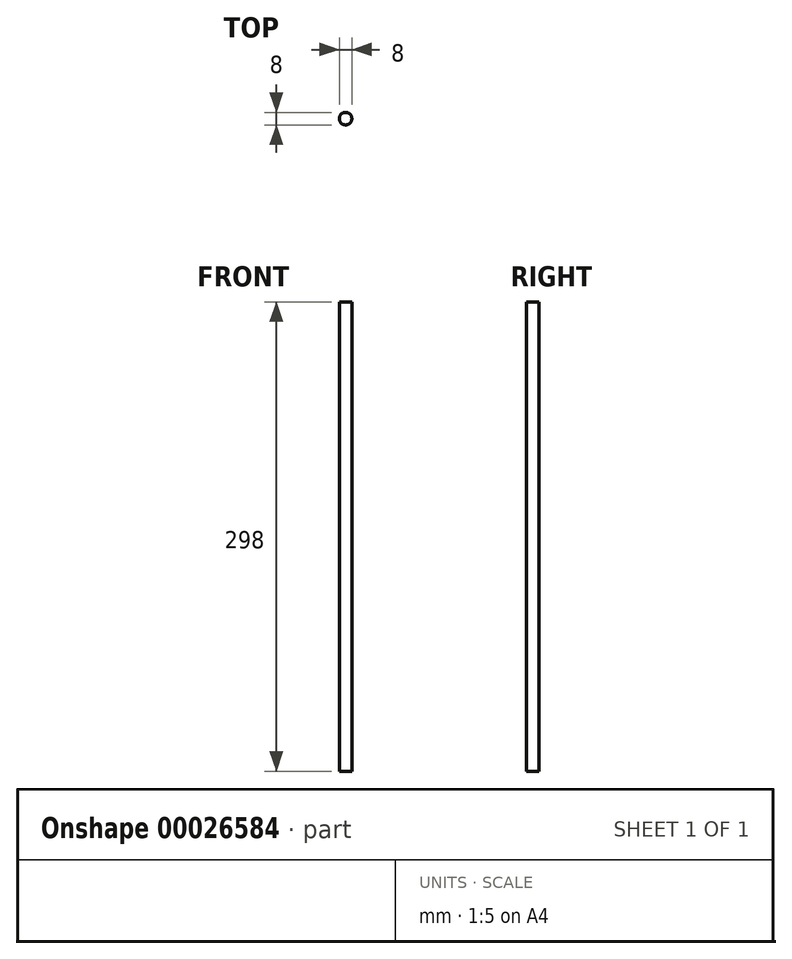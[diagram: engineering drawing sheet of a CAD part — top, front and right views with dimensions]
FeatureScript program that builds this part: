
annotation { "Feature Type Name" : "Feature", "Feature Type Description" : "" }
export const myFeature = defineFeature(function(context is Context, id is Id, definition is map)
    precondition{}
    {
        {
            var Q0;
            Q0=qCreatedBy(makeId("Top.planeOp"),FACE);
            var sketch = newSketch(context, id + "F0", { "sketchPlane" : qUnion([Q0])});
            skCircle(sketch, "E0", {"center": v(0, 0) * mm, "radius": 4 * mm});
            skSolve(sketch);
        }
        {
            var Q0;
            Q0=qSketchRegion(id+"F0",true);
            extrude(context, id + "F1", {"entities" : qUnion([Q0]), "depth" : 298 * mm});
        }
    });
